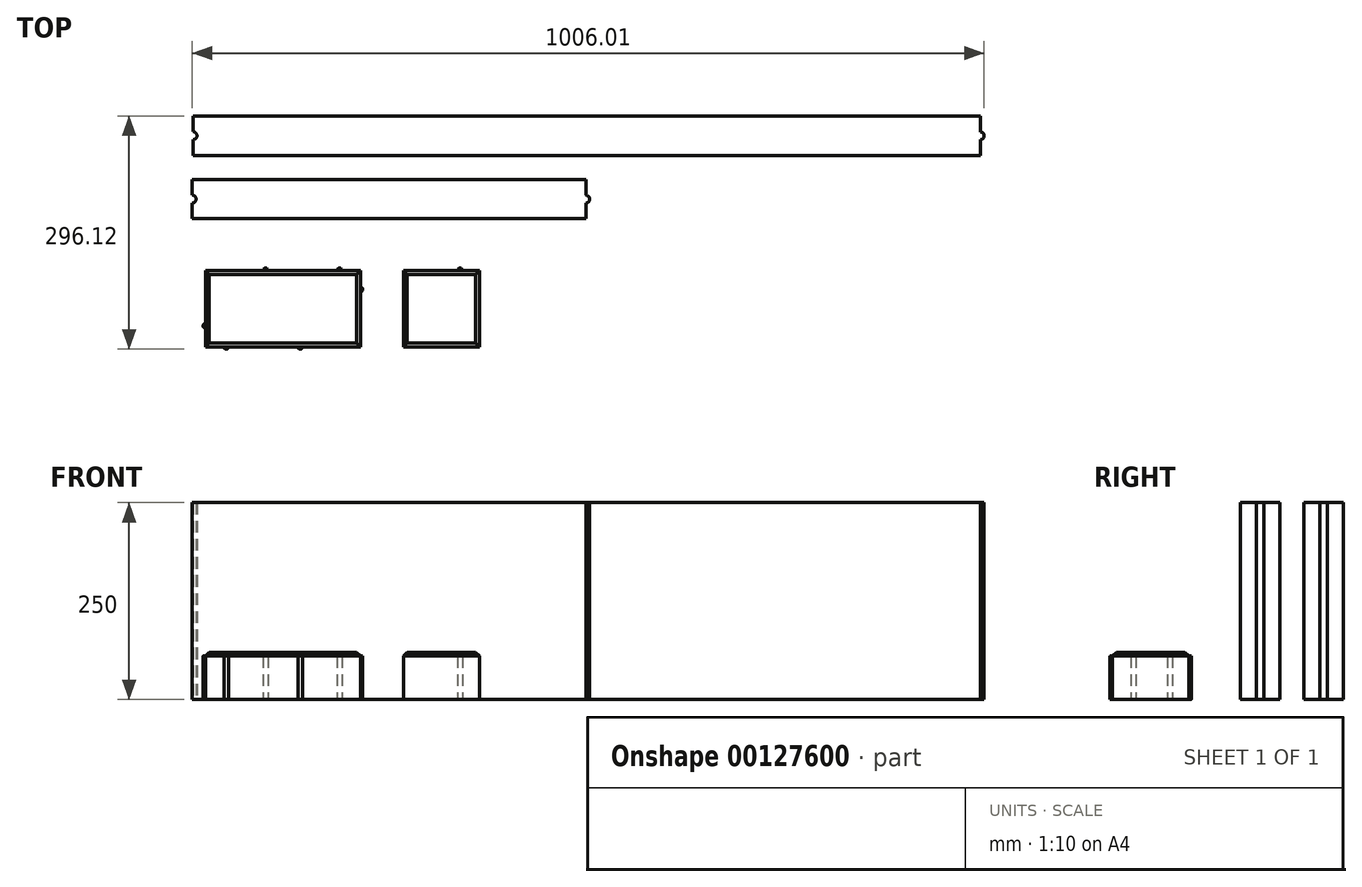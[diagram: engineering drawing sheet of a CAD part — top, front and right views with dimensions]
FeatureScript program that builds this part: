
annotation { "Feature Type Name" : "Feature", "Feature Type Description" : "" }
export const myFeature = defineFeature(function(context is Context, id is Id, definition is map)
    precondition{}
    {
        {
            var Q0;
            Q0=qCreatedBy(makeId("Top.planeOp"),FACE);
            var sketch = newSketch(context, id + "F0", { "sketchPlane" : qUnion([Q0])});
            skLineSegment(sketch, "E0", {"start": v(-547.66, 45.32) * mm, "end": v(452.34, 45.32) * mm});
            skLineSegment(sketch, "E1", {"start": v(452.34, 95.32) * mm, "end": v(-547.66, 95.32) * mm});
            skPoint(sketch, "E2.startSnap0", {"position": v(-547.66, 70.32) * mm});
            skArc(sketch, "E3", {"start": v(-547.66, 65.32) * mm, "mid": v(-542.66, 70.32) * mm, "end": v(-547.66, 75.32) * mm});
            skLineSegment(sketch, "E4", {"start": v(-547.66, 75.32) * mm, "end": v(-547.66, 95.32) * mm});
            skLineSegment(sketch, "E5", {"start": v(-547.66, 65.32) * mm, "end": v(-547.66, 45.32) * mm});
            skPoint(sketch, "E6.startSnap0", {"position": v(452.34, 70.32) * mm});
            skPoint(sketch, "E6.endSnap0", {"position": v(452.34, 70.32) * mm});
            skArc(sketch, "E7", {"start": v(452.34, 65.42) * mm, "mid": v(457.24, 70.32) * mm, "end": v(452.34, 75.22) * mm});
            skLineSegment(sketch, "E8", {"start": v(452.34, 95.32) * mm, "end": v(452.34, 75.22) * mm});
            skLineSegment(sketch, "E9", {"start": v(452.34, 65.42) * mm, "end": v(452.34, 45.32) * mm});
            skLineSegment(sketch, "E10", {"start": v(-548.77, -35.18) * mm, "end": v(-48.77, -35.18) * mm});
            skLineSegment(sketch, "E11", {"start": v(-48.77, 14.82) * mm, "end": v(-548.77, 14.82) * mm});
            skPoint(sketch, "E12.startSnap0", {"position": v(-548.77, -10.18) * mm});
            skArc(sketch, "E13", {"start": v(-548.77, -15.18) * mm, "mid": v(-543.77, -10.18) * mm, "end": v(-548.77, -5.18) * mm});
            skLineSegment(sketch, "E14", {"start": v(-548.77, -5.18) * mm, "end": v(-548.77, 14.82) * mm});
            skLineSegment(sketch, "E15", {"start": v(-548.77, -15.18) * mm, "end": v(-548.77, -35.18) * mm});
            skPoint(sketch, "E16.startSnap0", {"position": v(-48.77, -10.18) * mm});
            skPoint(sketch, "E16.endSnap0", {"position": v(451.23, -10.18) * mm});
            skArc(sketch, "E17", {"start": v(-48.77, -15.08) * mm, "mid": v(-43.87, -10.18) * mm, "end": v(-48.77, -5.28) * mm});
            skLineSegment(sketch, "E18", {"start": v(-48.77, 14.82) * mm, "end": v(-48.77, -5.28) * mm});
            skLineSegment(sketch, "E19", {"start": v(-48.77, -15.08) * mm, "end": v(-48.77, -35.18) * mm});
            skSolve(sketch);
        }
        {
            var Q0;
            Q0=makeQuery(id+"F0.imprint","IMPRINT",FACE,{"disambiguationData":[TD([[makeQuery(id+"F0.imprint","IMPRINT",EDGE,{"derivedFrom":sQuery(id+"F0.wireOp",EDGE,"E0")}),1.0]])]});
            var Q1;
            Q1=makeQuery(id+"F0.imprint","IMPRINT",FACE,{"disambiguationData":[TD([[makeQuery(id+"F0.imprint","IMPRINT",EDGE,{"derivedFrom":sQuery(id+"F0.wireOp",EDGE,"E10")}),1.0]])]});
            extrude(context, id + "F1", {"entities" : qUnion([Q0, Q1]), "depth" : 250 * mm});
        }
        {
            var Q0;
            Q0=qCreatedBy(makeId("Top.planeOp"),FACE);
            var sketch = newSketch(context, id + "F2", { "sketchPlane" : qUnion([Q0])});
            skLineSegment(sketch, "E20", {"start": v(-505.52, -186.22) * mm, "end": v(-505.52, -132.33) * mm, "construction": true});
            skLineSegment(sketch, "E21", {"start": v(-361.52, -127.85) * mm, "end": v(-361.52, -181.02) * mm, "construction": true});
            skLineSegment(sketch, "E22", {"start": v(-417.9, -124.85) * mm, "end": v(-471.9, -124.85) * mm, "construction": true});
            skLineSegment(sketch, "E23", {"start": v(-473.02, -171.3) * mm, "end": v(-414.55, -171.3) * mm, "construction": true});
            skArc(sketch, "E24", {"start": v(-508.52, -197.8) * mm, "mid": v(-505.52, -200.8) * mm, "end": v(-502.52, -197.8) * mm});
            skArc(sketch, "E25", {"start": v(-532.02, -174.3) * mm, "mid": v(-535.02, -171.3) * mm, "end": v(-532.02, -168.3) * mm});
            skArc(sketch, "E26", {"start": v(-335.02, -127.85) * mm, "mid": v(-332.02, -124.85) * mm, "end": v(-335.02, -121.85) * mm});
            skArc(sketch, "E27", {"start": v(-364.52, -100.8) * mm, "mid": v(-361.52, -97.8) * mm, "end": v(-358.52, -100.8) * mm});
            skLineSegment(sketch, "E28", {"start": v(-411.52, -161.9) * mm, "end": v(-411.52, -140.42) * mm, "construction": true});
            skLineSegment(sketch, "E29", {"start": v(-455.52, -160.85) * mm, "end": v(-455.52, -139.15) * mm, "construction": true});
            skArc(sketch, "E30", {"start": v(-452.52, -100.8) * mm, "mid": v(-455.52, -97.8) * mm, "end": v(-458.52, -100.8) * mm});
            skArc(sketch, "E31", {"start": v(-408.52, -197.8) * mm, "mid": v(-411.52, -200.8) * mm, "end": v(-414.52, -197.8) * mm});
            skLineSegment(sketch, "E32", {"start": v(-532.02, -197.8) * mm, "end": v(-508.52, -197.8) * mm});
            skLineSegment(sketch, "E33", {"start": v(-502.52, -197.8) * mm, "end": v(-414.52, -197.8) * mm});
            skLineSegment(sketch, "E34", {"start": v(-408.52, -197.8) * mm, "end": v(-335.02, -197.8) * mm});
            skLineSegment(sketch, "E35", {"start": v(-532.02, -197.8) * mm, "end": v(-532.02, -174.3) * mm});
            skLineSegment(sketch, "E36", {"start": v(-532.02, -168.3) * mm, "end": v(-532.02, -100.8) * mm});
            skLineSegment(sketch, "E37", {"start": v(-532.02, -100.8) * mm, "end": v(-458.52, -100.8) * mm});
            skLineSegment(sketch, "E38", {"start": v(-452.52, -100.8) * mm, "end": v(-364.52, -100.8) * mm});
            skLineSegment(sketch, "E39", {"start": v(-358.52, -100.8) * mm, "end": v(-335.02, -100.8) * mm});
            skLineSegment(sketch, "E40", {"start": v(-335.02, -100.8) * mm, "end": v(-335.02, -121.85) * mm});
            skLineSegment(sketch, "E41", {"start": v(-335.02, -127.85) * mm, "end": v(-335.02, -197.8) * mm});
            skLineSegment(sketch, "E42", {"start": v(-364.52, -100.8) * mm, "end": v(-358.52, -100.8) * mm, "construction": true});
            skLineSegment(sketch, "E43.bottom", {"start": v(-280.6, -197.8) * mm, "end": v(-183.6, -197.8) * mm});
            skLineSegment(sketch, "E43.top", {"start": v(-280.6, -100.8) * mm, "end": v(-183.6, -100.8) * mm});
            skLineSegment(sketch, "E43.left", {"start": v(-280.6, -197.8) * mm, "end": v(-280.6, -100.8) * mm});
            skLineSegment(sketch, "E43.right", {"start": v(-183.6, -197.8) * mm, "end": v(-183.6, -100.8) * mm});
            skArc(sketch, "E44", {"start": v(-280.6, -174.3) * mm, "mid": v(-283.6, -171.3) * mm, "end": v(-280.6, -168.3) * mm});
            skArc(sketch, "E45", {"start": v(-183.6, -121.85) * mm, "mid": v(-180.6, -124.85) * mm, "end": v(-183.6, -127.85) * mm});
            skLineSegment(sketch, "E46", {"start": v(-255.6, -133.35) * mm, "end": v(-255.6, -164.63) * mm, "construction": true});
            skLineSegment(sketch, "E47", {"start": v(-208.6, -132.39) * mm, "end": v(-208.6, -159.64) * mm, "construction": true});
            skArc(sketch, "E48", {"start": v(-252.6, -197.8) * mm, "mid": v(-255.6, -200.8) * mm, "end": v(-258.6, -197.8) * mm});
            skArc(sketch, "E49", {"start": v(-205.6, -100.8) * mm, "mid": v(-208.6, -97.8) * mm, "end": v(-211.6, -100.8) * mm});
            skSolve(sketch);
        }
        {
            var Q0;
            Q0=makeQuery(id+"F2.imprint","IMPRINT",FACE,{"disambiguationData":[TD([[makeQuery(id+"F2.imprint","IMPRINT",EDGE,{"derivedFrom":sQuery(id+"F2.wireOp",EDGE,"E24")}),1.0]])]});
            var Q1;
            Q1=makeQuery(id+"F2.imprint","IMPRINT",FACE,{"disambiguationData":[TD([[makeQuery(id+"F2.imprint","IMPRINT",EDGE,{"derivedFrom":sQuery(id+"F2.wireOp",EDGE,"1FTHRRi8-SAsX-ipau-ZrRI-a4Fst7Mu8mG8")}),-1.0]])]});
            var Q2;
            {var subQ0=sQuery(id+"F2.wireOp",EDGE,"E43.left");var subQ7=sQuery(id+"F2.wireOp",EDGE,"E43.bottom");var subQ15=makeQuery(id+"F2.imprint","INTERSECT",VERTEX,{"derivedFrom":[subQ7,subQ0]});Q2=makeQuery(id+"F2.imprint","IMPRINT",FACE,{"disambiguationData":[TD([[makeQuery(id+"F2.imprint","IMPRINT",EDGE,{"disambiguationData":[TD([[subQ15,-1.0]])],"derivedFrom":subQ7}),1.0]])]});}
            var Q3;
            {var subQ0=sQuery(id+"F2.wireOp",EDGE,"E44");Q3=makeQuery(id+"F2.imprint","IMPRINT",FACE,{"disambiguationData":[TD([[makeQuery(id+"F2.imprint","IMPRINT",EDGE,{"derivedFrom":subQ0}),-1.0]])]});}
            var Q4;
            {var subQ0=sQuery(id+"F2.wireOp",EDGE,"E48");Q4=makeQuery(id+"F2.imprint","IMPRINT",FACE,{"disambiguationData":[TD([[makeQuery(id+"F2.imprint","IMPRINT",EDGE,{"derivedFrom":subQ0}),-1.0]])]});}
            var Q5;
            {var subQ0=sQuery(id+"F2.wireOp",EDGE,"E45");Q5=makeQuery(id+"F2.imprint","IMPRINT",FACE,{"disambiguationData":[TD([[makeQuery(id+"F2.imprint","IMPRINT",EDGE,{"derivedFrom":subQ0}),-1.0]])]});}
            var Q6;
            {var subQ0=sQuery(id+"F2.wireOp",EDGE,"E49");Q6=makeQuery(id+"F2.imprint","IMPRINT",FACE,{"disambiguationData":[TD([[makeQuery(id+"F2.imprint","IMPRINT",EDGE,{"derivedFrom":subQ0}),1.0]])]});}
            extrude(context, id + "F3", {"entities" : qUnion([Q0, Q1, Q2, Q3, Q4, Q5, Q6]), "depth" : 55 * mm});
        }
        {
            var Q0;
            Q0=makeQuery(id+"F3.opExtrude","CAP_FACE",FACE,{"disambiguationData":[OSD([sQuery(id+"F2.wireOp",EDGE,"E24"),sQuery(id+"F2.wireOp",EDGE,"E25"),sQuery(id+"F2.wireOp",EDGE,"E26"),sQuery(id+"F2.wireOp",EDGE,"E27"),sQuery(id+"F2.wireOp",EDGE,"E30"),sQuery(id+"F2.wireOp",EDGE,"E31"),sQuery(id+"F2.wireOp",EDGE,"E32"),sQuery(id+"F2.wireOp",EDGE,"E33"),sQuery(id+"F2.wireOp",EDGE,"E34"),sQuery(id+"F2.wireOp",EDGE,"E35"),sQuery(id+"F2.wireOp",EDGE,"E36"),sQuery(id+"F2.wireOp",EDGE,"E37"),sQuery(id+"F2.wireOp",EDGE,"E38"),sQuery(id+"F2.wireOp",EDGE,"E39"),sQuery(id+"F2.wireOp",EDGE,"E40"),sQuery(id+"F2.wireOp",EDGE,"E41")])],"isStart":false});
            var sketch = newSketch(context, id + "F4", { "sketchPlane" : qUnion([Q0])});
            skLineSegment(sketch, "E50", {"start": v(-532.02, -168.3) * mm, "end": v(-532.02, -174.3) * mm});
            skLineSegment(sketch, "E51", {"start": v(-508.52, -197.8) * mm, "end": v(-502.52, -197.8) * mm});
            skLineSegment(sketch, "E52", {"start": v(-414.52, -197.8) * mm, "end": v(-408.52, -197.8) * mm});
            skLineSegment(sketch, "E53", {"start": v(-335.02, -127.85) * mm, "end": v(-335.02, -121.85) * mm});
            skLineSegment(sketch, "E54", {"start": v(-358.52, -100.8) * mm, "end": v(-364.52, -100.8) * mm});
            skLineSegment(sketch, "E55", {"start": v(-458.52, -100.8) * mm, "end": v(-452.52, -100.8) * mm});
            skSolve(sketch);
        }
        {
            var Q0;
            Q0=makeQuery(id+"F4.imprint","IMPRINT",FACE,{"disambiguationData":[TD([[makeQuery(id+"F4.imprint","IMPRINT",EDGE,{"derivedFrom":sQuery(id+"F4.wireOp",EDGE,"E50")}),1.0]])]});
            extrude(context, id + "F5", {"entities" : qUnion([Q0]), "operationType" : NewBodyOperationType.ADD, "depth" : 5 * mm});
        }
        {
            var Q0;
            Q0=makeQuery(id+"F5.opExtrude","CAP_FACE",FACE,{"disambiguationData":[OSD([sQuery(id+"F2.wireOp",EDGE,"E32"),sQuery(id+"F2.wireOp",EDGE,"E33"),sQuery(id+"F2.wireOp",EDGE,"E34"),sQuery(id+"F2.wireOp",EDGE,"E35"),sQuery(id+"F2.wireOp",EDGE,"E36"),sQuery(id+"F2.wireOp",EDGE,"E37"),sQuery(id+"F2.wireOp",EDGE,"E38"),sQuery(id+"F2.wireOp",EDGE,"E39"),sQuery(id+"F2.wireOp",EDGE,"E40"),sQuery(id+"F2.wireOp",EDGE,"E41"),sQuery(id+"F4.wireOp",EDGE,"E50"),sQuery(id+"F4.wireOp",EDGE,"E51"),sQuery(id+"F4.wireOp",EDGE,"E52"),sQuery(id+"F4.wireOp",EDGE,"E53"),sQuery(id+"F4.wireOp",EDGE,"E54"),sQuery(id+"F4.wireOp",EDGE,"E55")])],"isStart":false});
            chamfer(context, id + "F6", {"entities" : qUnion([Q0]), "width" : 5 * mm, "tangentPropagation" : true});
        }
        {
            var Q0;
            Q0=makeQuery(id+"F3.opExtrude","CAP_FACE",FACE,{"disambiguationData":[OSD([sQuery(id+"F2.wireOp",EDGE,"E43.bottom"),sQuery(id+"F2.wireOp",EDGE,"E43.top"),sQuery(id+"F2.wireOp",EDGE,"E43.left"),sQuery(id+"F2.wireOp",EDGE,"E43.right"),sQuery(id+"F2.wireOp",EDGE,"E44"),sQuery(id+"F2.wireOp",EDGE,"E45"),sQuery(id+"F2.wireOp",EDGE,"E48"),sQuery(id+"F2.wireOp",EDGE,"E49")])],"isStart":false});
            var sketch = newSketch(context, id + "F7", { "sketchPlane" : qUnion([Q0])});
            skLineSegment(sketch, "E56", {"start": v(-280.6, -174.3) * mm, "end": v(-280.6, -168.3) * mm});
            skLineSegment(sketch, "E57", {"start": v(-258.6, -197.8) * mm, "end": v(-252.6, -197.8) * mm});
            skLineSegment(sketch, "E58", {"start": v(-183.6, -127.85) * mm, "end": v(-183.6, -121.85) * mm});
            skLineSegment(sketch, "E59", {"start": v(-205.6, -100.8) * mm, "end": v(-211.6, -100.8) * mm});
            skSolve(sketch);
        }
        {
            var Q0;
            Q0=makeQuery(id+"F7.imprint","IMPRINT",FACE,{"disambiguationData":[TD([[makeQuery(id+"F7.imprint","IMPRINT",EDGE,{"derivedFrom":sQuery(id+"F7.wireOp",EDGE,"E56")}),-1.0]])]});
            extrude(context, id + "F8", {"entities" : qUnion([Q0]), "operationType" : NewBodyOperationType.ADD, "depth" : 5 * mm});
        }
        {
            var Q0;
            Q0=makeQuery(id+"F8.opExtrude","CAP_FACE",FACE,{"disambiguationData":[OSD([sQuery(id+"F2.wireOp",EDGE,"E43.bottom"),sQuery(id+"F2.wireOp",EDGE,"E43.top"),sQuery(id+"F2.wireOp",EDGE,"E43.left"),sQuery(id+"F2.wireOp",EDGE,"E43.right"),sQuery(id+"F7.wireOp",EDGE,"E56"),sQuery(id+"F7.wireOp",EDGE,"E57"),sQuery(id+"F7.wireOp",EDGE,"E58"),sQuery(id+"F7.wireOp",EDGE,"E59")])],"isStart":false});
            chamfer(context, id + "F9", {"entities" : qUnion([Q0]), "width" : 5 * mm, "tangentPropagation" : true});
        }
    });
